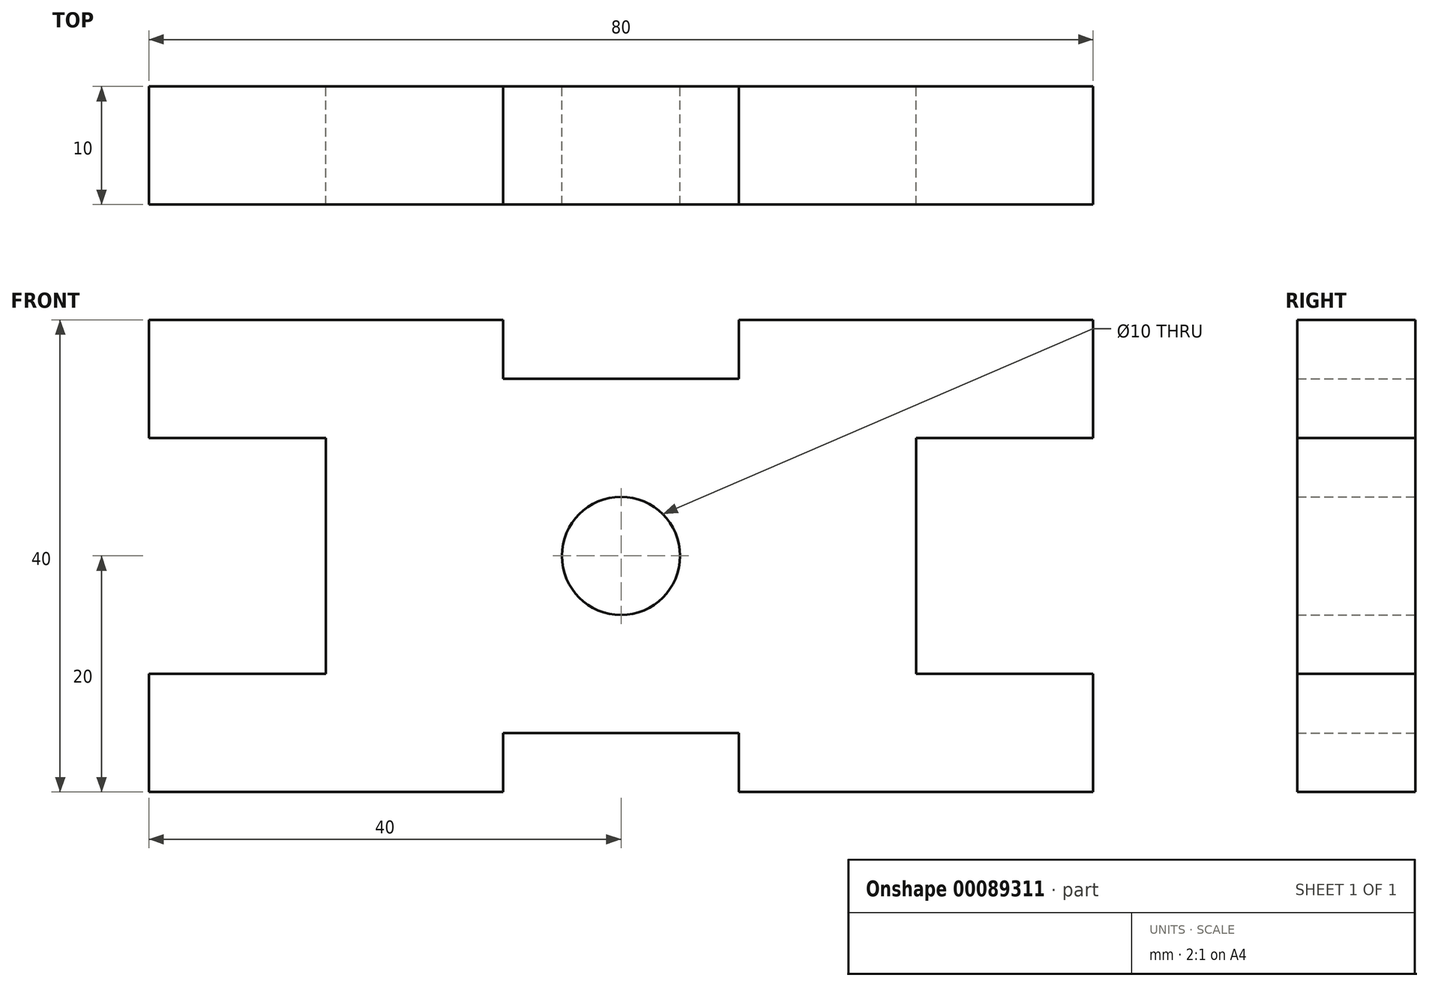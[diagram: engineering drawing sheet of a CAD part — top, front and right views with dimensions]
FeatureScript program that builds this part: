
annotation { "Feature Type Name" : "Feature", "Feature Type Description" : "" }
export const myFeature = defineFeature(function(context is Context, id is Id, definition is map)
    precondition{}
    {
        {
            var Q0;
            Q0=qCreatedBy(makeId("Front.planeOp"),FACE);
            var sketch = newSketch(context, id + "F0", { "sketchPlane" : qUnion([Q0])});
            skCircle(sketch, "E0", {"center": v(0, 0) * mm, "radius": 5 * mm});
            skLineSegment(sketch, "E1", {"start": v(10, 15) * mm, "end": v(10, 20) * mm});
            skLineSegment(sketch, "E2", {"start": v(10, 20) * mm, "end": v(40, 20) * mm});
            skLineSegment(sketch, "E3", {"start": v(40, 20) * mm, "end": v(40, 10) * mm});
            skLineSegment(sketch, "E4", {"start": v(40, 10) * mm, "end": v(25, 10) * mm});
            skLineSegment(sketch, "E5", {"start": v(25, -10) * mm, "end": v(40, -10) * mm});
            skLineSegment(sketch, "E6", {"start": v(40, -10) * mm, "end": v(40, -20) * mm});
            skLineSegment(sketch, "E7", {"start": v(40, -20) * mm, "end": v(10, -20) * mm});
            skLineSegment(sketch, "E8", {"start": v(10, -20) * mm, "end": v(10, -15) * mm});
            skLineSegment(sketch, "E9", {"start": v(-10, -15) * mm, "end": v(-10, -20) * mm});
            skLineSegment(sketch, "E10", {"start": v(-10, -20) * mm, "end": v(-40, -20) * mm});
            skLineSegment(sketch, "E11", {"start": v(-40, -20) * mm, "end": v(-40, -10) * mm});
            skLineSegment(sketch, "E12", {"start": v(-40, -10) * mm, "end": v(-25, -10) * mm});
            skLineSegment(sketch, "E13", {"start": v(-25, 10) * mm, "end": v(-40, 10) * mm});
            skLineSegment(sketch, "E14", {"start": v(-40, 10) * mm, "end": v(-40, 20) * mm});
            skLineSegment(sketch, "E15", {"start": v(-40, 20) * mm, "end": v(-10, 20) * mm});
            skLineSegment(sketch, "E16", {"start": v(-10, 20) * mm, "end": v(-10, 15) * mm});
            skLineSegment(sketch, "E17", {"start": v(25, 10) * mm, "end": v(25, 0) * mm});
            skLineSegment(sketch, "E18", {"start": v(25, 0) * mm, "end": v(25, -10) * mm});
            skLineSegment(sketch, "E19", {"start": v(-25, 10) * mm, "end": v(-25, 0) * mm});
            skLineSegment(sketch, "E20", {"start": v(-25, 0) * mm, "end": v(-25, -10) * mm});
            skLineSegment(sketch, "E21", {"start": v(-10, -15) * mm, "end": v(0, -15) * mm});
            skLineSegment(sketch, "E22", {"start": v(0, -15) * mm, "end": v(10, -15) * mm});
            skLineSegment(sketch, "E23", {"start": v(-10, 15) * mm, "end": v(0, 15) * mm});
            skLineSegment(sketch, "E24", {"start": v(0, 15) * mm, "end": v(10, 15) * mm});
            skSolve(sketch);
        }
        {
            var Q0;
            Q0 = qSketchRegion(id + "F0", true);
            extrude(context, id + "F1", {"entities" : qUnion([Q0]), "depth" : 10 * mm});
        }
    });
